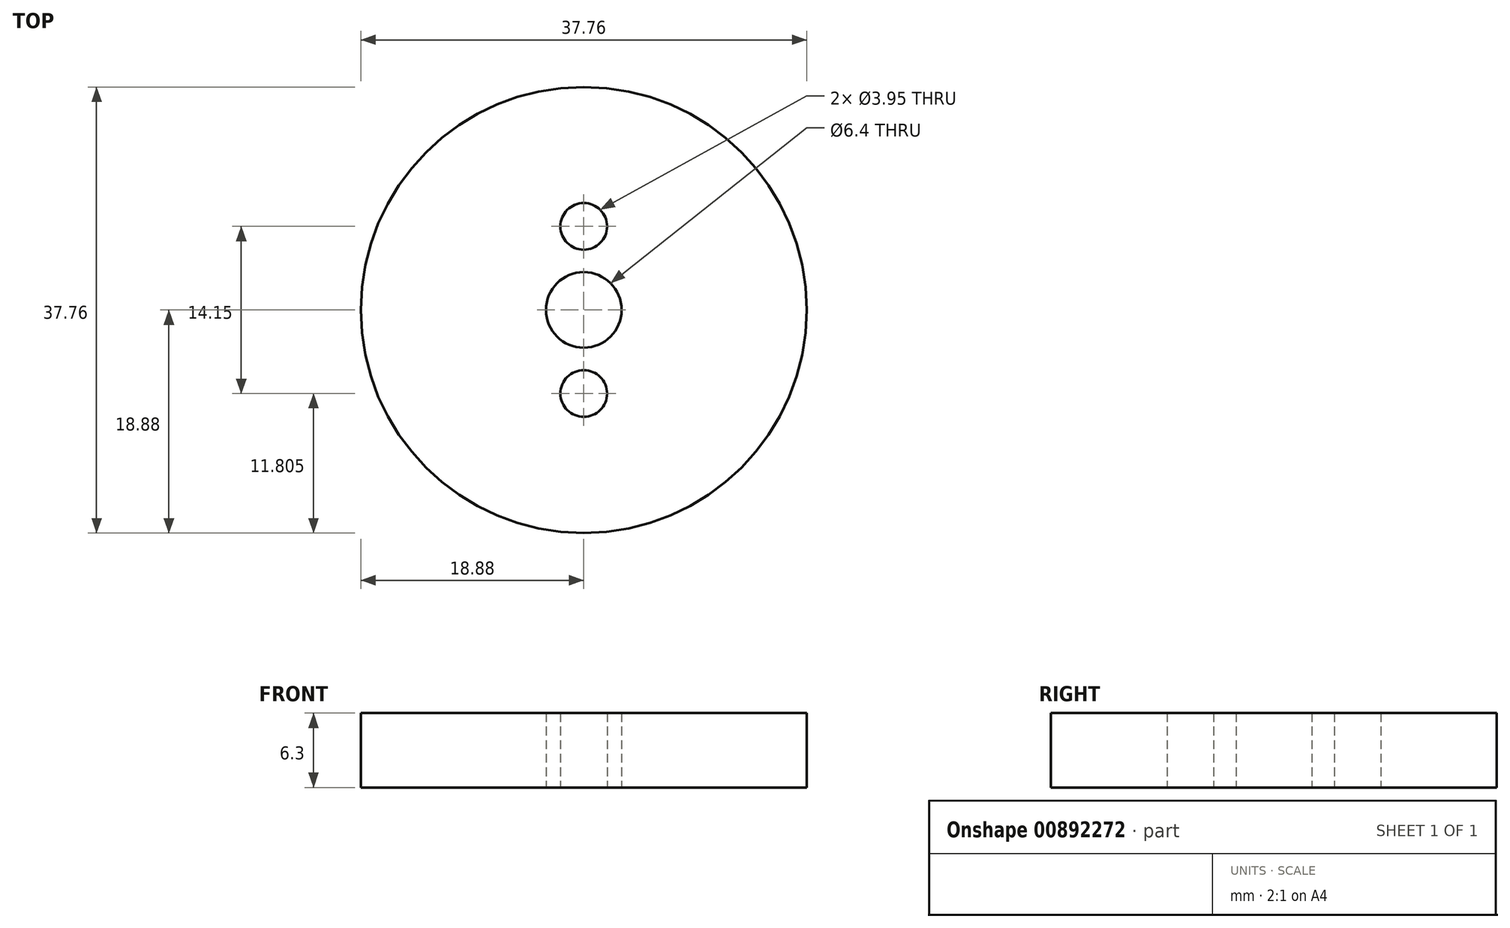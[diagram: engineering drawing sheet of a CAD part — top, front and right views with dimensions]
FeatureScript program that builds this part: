
annotation { "Feature Type Name" : "Feature", "Feature Type Description" : "" }
export const myFeature = defineFeature(function(context is Context, id is Id, definition is map)
    precondition{}
    {
        {
            var Q0;
            Q0=qCreatedBy(makeId("Top.planeOp"),FACE);
            var sketch = newSketch(context, id + "F0", { "sketchPlane" : qUnion([Q0])});
            skCircle(sketch, "E0", {"center": v(0, 0) * mm, "radius": 18.88 * mm});
            skCircle(sketch, "E1", {"center": v(0, -7.08) * mm, "radius": 1.98 * mm});
            skCircle(sketch, "E2", {"center": v(0, 7.08) * mm, "radius": 1.98 * mm});
            skSolve(sketch);
        }
        {
            var Q0;
            Q0 = qSketchRegion(id + "F0", true);
            extrude(context, id + "F1", {"entities" : qUnion([Q0]), "depth" : 6.3 * mm, "offsetDistance" : 25 * mm});
        }
        {
            var Q0;
            Q0=sQuery(id+"F0.wireOp",VERTEX,"E0.center");
            var Q1;
            Q1=makeQuery(id+"F1.opExtrude","SWEPT_BODY",BODY,{"disambiguationData":[OSD([sQuery(id+"F0.wireOp",EDGE,"E0")])]});
            hole(context, id + "F2", {"style" : HoleStyle.SIMPLE, "endStyle" : HoleEndStyle.THROUGH, "oppositeDirection" : true, "holeDiameter" : 6.4 * mm, "majorDiameter" : 5 * mm, "isTappedThrough" : true, "tappedDepth" : 12 * mm, "tapClearance" : 3, "locations" : qUnion([Q0]), "scope" : qUnion([Q1])});
        }
    });
